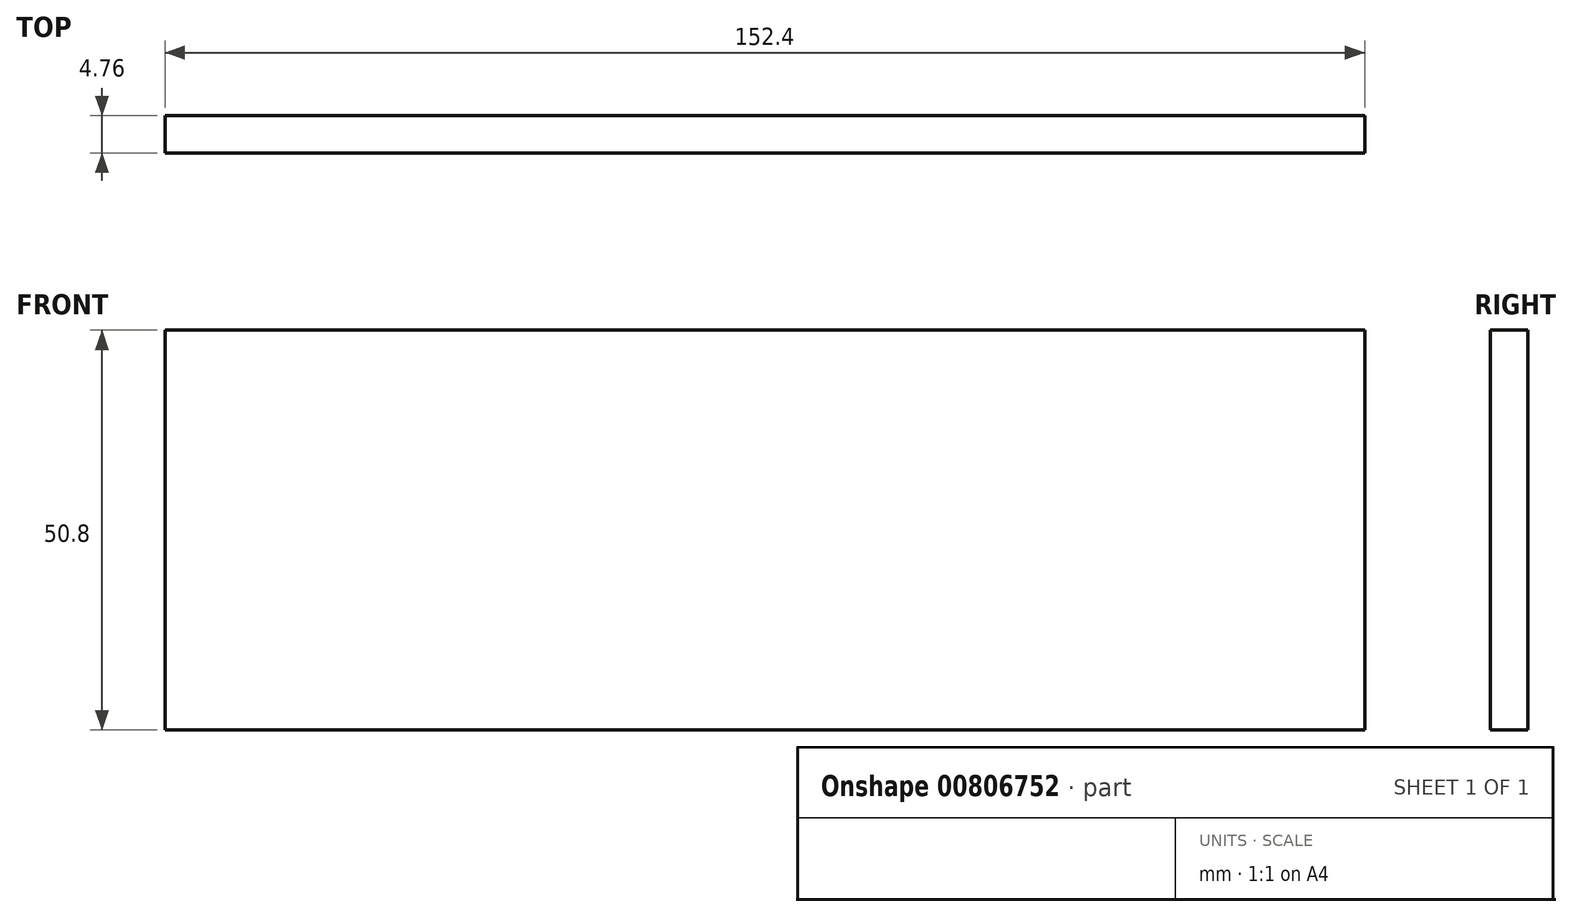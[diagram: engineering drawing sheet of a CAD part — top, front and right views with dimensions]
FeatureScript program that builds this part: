
annotation { "Feature Type Name" : "Feature", "Feature Type Description" : "" }
export const myFeature = defineFeature(function(context is Context, id is Id, definition is map)
    precondition{}
    {
        {
            var Q0;
            Q0=qCreatedBy(makeId("Front.planeOp"),FACE);
            var sketch = newSketch(context, id + "F0", { "sketchPlane" : qUnion([Q0])});
            skLineSegment(sketch, "E0.bottom", {"start": v(0, 0) * mm, "end": v(152.4, 0) * mm});
            skLineSegment(sketch, "E0.top", {"start": v(0, 50.8) * mm, "end": v(152.4, 50.8) * mm});
            skLineSegment(sketch, "E0.left", {"start": v(0, 0) * mm, "end": v(0, 50.8) * mm});
            skLineSegment(sketch, "E0.right", {"start": v(152.4, 0) * mm, "end": v(152.4, 50.8) * mm});
            skSolve(sketch);
        }
        {
            var Q0;
            Q0 = qSketchRegion(id + "F0", true);
            extrude(context, id + "F1", {"entities" : qUnion([Q0]), "depth" : 4.76 * mm, "offsetDistance" : 25.4 * mm});
        }
    });
